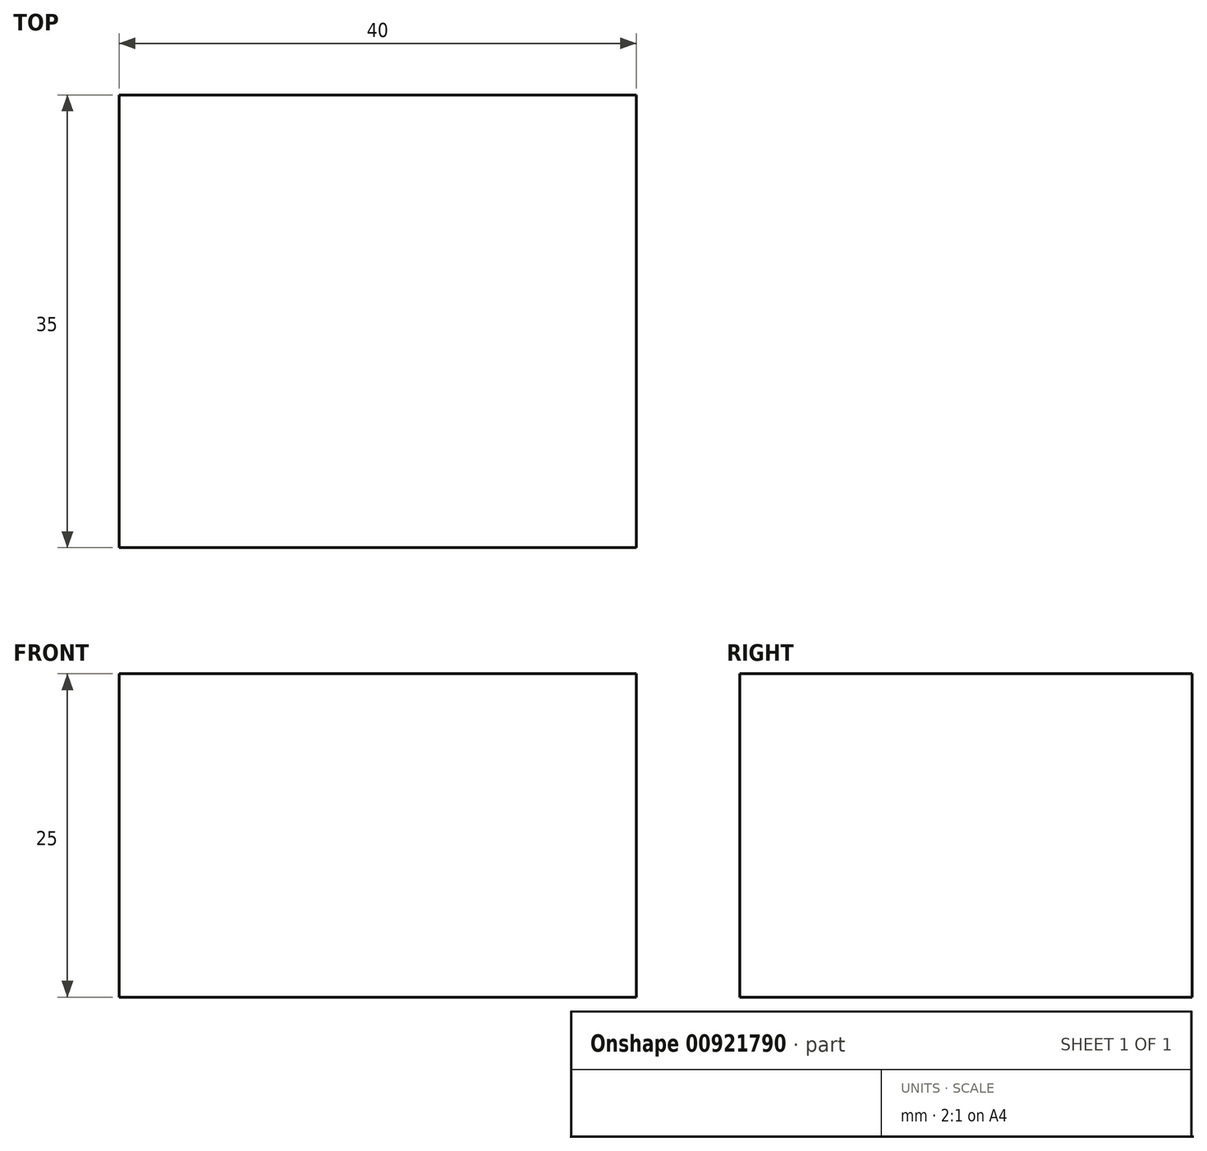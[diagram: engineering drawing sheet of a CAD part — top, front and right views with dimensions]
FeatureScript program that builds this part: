
annotation { "Feature Type Name" : "Feature", "Feature Type Description" : "" }
export const myFeature = defineFeature(function(context is Context, id is Id, definition is map)
    precondition{}
    {
        {
            var Q0;
            Q0=qCreatedBy(makeId("Top.planeOp"),FACE);
            var sketch = newSketch(context, id + "F0", { "sketchPlane" : qUnion([Q0])});
            skLineSegment(sketch, "E0.bottom", {"start": v(0, 0) * mm, "end": v(-40, 0) * mm});
            skLineSegment(sketch, "E0.top", {"start": v(0, -35) * mm, "end": v(-40, -35) * mm});
            skLineSegment(sketch, "E0.left", {"start": v(0, 0) * mm, "end": v(0, -35) * mm});
            skLineSegment(sketch, "E0.right", {"start": v(-40, 0) * mm, "end": v(-40, -35) * mm});
            skSolve(sketch);
        }
        {
            var Q0;
            Q0 = qSketchRegion(id + "F0", true);
            extrude(context, id + "F1", {"entities" : qUnion([Q0]), "depth" : 25 * mm, "offsetDistance" : 25 * mm});
        }
    });
